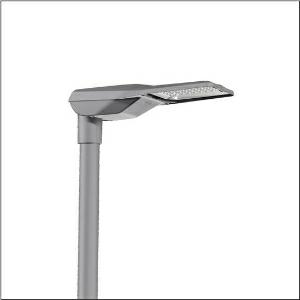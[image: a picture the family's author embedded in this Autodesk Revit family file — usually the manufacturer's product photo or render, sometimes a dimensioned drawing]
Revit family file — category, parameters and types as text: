
# Revit family: streetlight_sl_21_iq_mini___p0_5a_5xe2v31d08hb_68d8
name_source: partatom
category: Lighting Fixtures
units: mm (PartAtom-declared; Revit-internal decimal feet)

## family parameters
Cut with Voids When Loaded = No
Host = Face
Light Source = No
Part Type = Normal
Room Calculation Point = No
Round Connector Dimension = Use Diameter
Shared = No

## types (1)
- --- (1 x LED, 9290 lm, 70.9 W, 3000K)
    Apparent Load = 71 VA
    CIE Flux Codes = 37 73 96 100 100
    Color Rendering = 70
    Color Temperature = 3000K
    Default Elevation = 1800 mm
    Description = Streetlight SL 21 iQ mini, mast luminaire, primary light control with lens, of PMMA, primary optical cover: cover, of toughened safety glass, transparent, light distribution: P0.5a, light emission: direct distribution, primary light characteristic: asymmetric, installation type: post-top, side-entry, LED, High Power LED, rated luminous flux: 9.290lm, luminous efficacy: 131lm/W, light colour: 730, colour temperature: 3000K, control gear: iQ-Comfort, control: pre-setting: linear dimming characteristic, Auto-Match, Temp-Guard, Lumen-Switch, Night-Set, Smart-Wire, Light-Fading, Desk-Remote (wireless, voltage-free reading and setting of iQ features in the workshop via application-optimized NFC function/RFID function), optimised constant luminous flux control (CLO 2.0), mains connection: 220..240V, AC, 50/60Hz, start of lifetime: 71W, end of service life: 75W, reduction: 31W, luminaire housing, of diecast aluminium, powder-coated, Siteco® metallic grey (DB 702S), corrosivity category C5 mid according to DIN EN ISO 12944, please order mast flange separately, inclination adjustable: 0°, 5°, 10°, 15°, sealing non-destructively replaceable, multi-level sealing system, length: 628mm, width: 235mm, height: 110mm, mast flange for spigot size: 42mm (side-entry): 5XC10008XM4, 60/48mm (side-entry/post-top): 5XC10108XM2, 76/60mm (side-entry/post-top): 5XC10108XM1, mounting height: 4..8m, protection rating (complete): IP66, insulation class (complete): insulation class II (safety insulation), certification: CE, ENEC, ENEC+, VDE, impact resistance: IK10, permissible operating ambient temperature for outdoor applications: -40..+50°C, standard-compliant lighting for roads and squares, packaging unit: 1 piece

Light Distribution: P0.5a
    Height = 110 mm
    Lamp = 1 x LED
    Lamp Light Flux = 9290 lm
    Lamp Power = 70.9 W
    Lamp count = 1
    Length = 625 mm
    Luminous efficacy = 131 lm/W
    Manufacturer = Siteco
    ModVariant = No
    Model = 5XE2V31D08HB
    Number of Poles = 1
    OnlyDefault = Yes
    Power Factor = 1
    Product Name = Streetlight SL 21 iQ mini | P0.5a
    Product group = mast luminaire | pylon top
    ProductGroupID = 6100
    Protection Class = Protection class II
    Protection Degree = IP 66
    RLX_Detail_Level = 1
    RLX_Emergency_Light_Flux = 0 lm
    RLX_Emergency_Type = 0
    RLX_Emergency_Type_DB = No
    RlxData = <blob elided: 91813 chars, md5=a153e04e>
    Socket = socket
    Standby Power = 0 W
    System Light Flux = 9290 lm
    System Power = 71 W
    Type Comments = factory setting: luminous flux: 100 % | dim-lin: 254 | 711 mA
    Type Image = l_1003519.jpg
    URL = http://relux.com
    VarID = @adj_091253
    Voltage = 0 V
    Weight = 0.00 kg
    Width = 234 mm

## geometry (parser evidence)
native form markers: Blend x4, Sweep x12
no freeform markers — native parametric forms only
